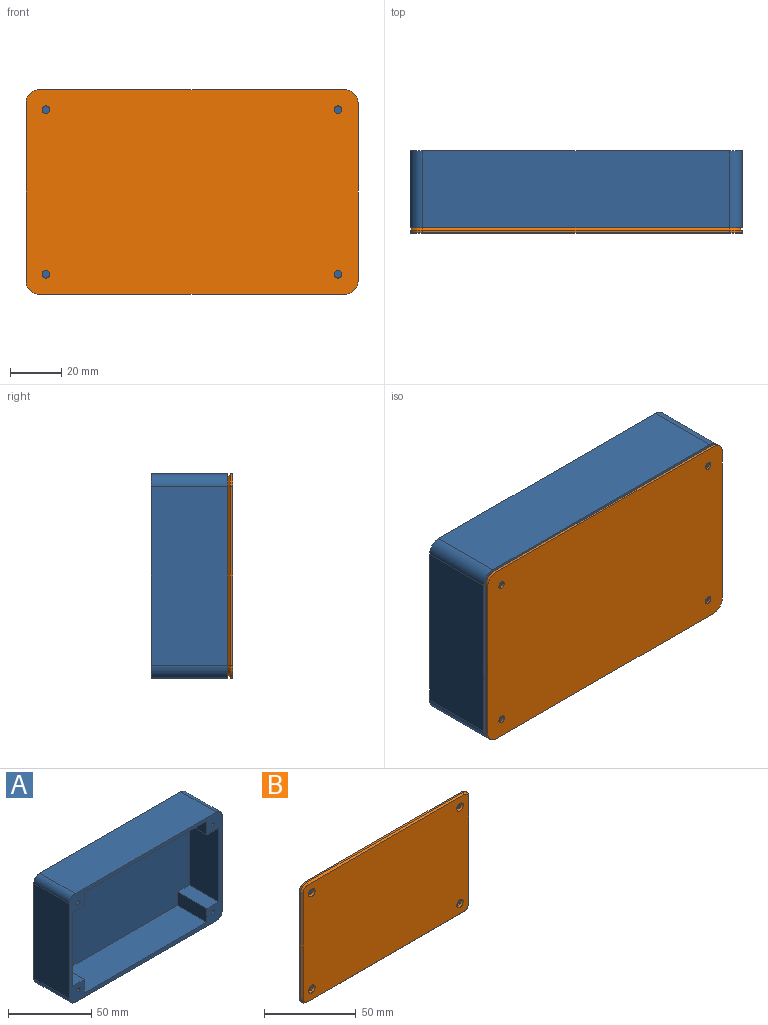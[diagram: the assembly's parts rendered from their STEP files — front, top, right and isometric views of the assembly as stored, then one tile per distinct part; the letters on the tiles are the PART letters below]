
ASSEMBLY  parts=2 mates=1
PART A: 31 faces, bbox 130x30x80 mm
  f0: plane 25x10mm, normal (1,0,0), area 250mm2, adj f1,f2,f5,f6
  f1: plane 25x10mm, normal (0,0,1), area 250mm2, adj f0,f2,f6,f21
  f2: plane 130x80mm, normal (0,-1,0), area 1494.9mm2, adj f0,f1,f3,f5,f7,f8,f9,f11
  f3: cylinder r=1.5mm len=10mm, axis (0,-1,0), area 94.2mm2, adj f2,f4
  f4: plane 3x3mm, normal (0,-1,0), area 7.1mm2, adj f3
  f5: plane 104.4x25mm, normal (0,0,1), area 2610mm2, adj f0,f2,f6,f12
  f6: plane 124.4x74.4mm, normal (0,-1,0), area 8855.4mm2, adj f0,f1,f5,f7,f8,f11,f12,f13
  f7: plane 25x10mm, normal (-1,0,0), area 250mm2, adj f2,f6,f8,f20
  f8: plane 25x10mm, normal (0,0,-1), area 250mm2, adj f2,f6,f7,f11
  f9: cylinder r=1.5mm len=10mm, axis (0,-1,0), area 94.2mm2, adj f2,f10
  f10: plane 3x3mm, normal (0,-1,0), area 7.1mm2, adj f9
  f11: plane 54.4x25mm, normal (-1,0,0), area 1360mm2, adj f2,f6,f8,f13
  f12: plane 25x10mm, normal (-1,0,0), area 250mm2, adj f2,f5,f6,f13
  f13: plane 25x10mm, normal (0,0,1), area 250mm2, adj f2,f6,f11,f12
  f14: cylinder r=1.5mm len=10mm, axis (0,-1,0), area 94.2mm2, adj f2,f15
  f15: plane 3x3mm, normal (0,-1,0), area 7.1mm2, adj f14
  f16: plane 25x10mm, normal (1,0,0), area 250mm2, adj f2,f6,f17,f20
  f17: plane 25x10mm, normal (0,0,-1), area 250mm2, adj f2,f6,f16,f21
  f18: cylinder r=1.5mm len=10mm, axis (0,-1,0), area 94.2mm2, adj f2,f19
  f19: plane 3x3mm, normal (0,-1,0), area 7.1mm2, adj f18
  f20: plane 104.4x25mm, normal (0,0,-1), area 2610mm2, adj f2,f6,f7,f16
  f21: plane 54.4x25mm, normal (1,0,0), area 1360mm2, adj f1,f2,f6,f17
  f22: cylinder r=5mm len=30mm, axis (0,1,0), area 235.6mm2, adj f2,f23,f29,f30
  f23: plane 120x30mm, normal (0,0,-1), area 3600mm2, adj f2,f22,f24,f30
  f24: cylinder r=5mm len=30mm, axis (0,1,0), area 235.6mm2, adj f2,f23,f25,f30
  f25: plane 70x30mm, normal (1,0,0), area 2100mm2, adj f2,f24,f26,f30
  f26: cylinder r=5mm len=30mm, axis (0,1,0), area 235.6mm2, adj f2,f25,f27,f30
  f27: plane 120x30mm, normal (0,0,1), area 3600mm2, adj f2,f26,f28,f30
  f28: cylinder r=5mm len=30mm, axis (0,1,0), area 235.6mm2, adj f2,f27,f29,f30
  f29: plane 70x30mm, normal (-1,0,0), area 2100mm2, adj f2,f22,f28,f30
  f30: plane 130x80mm, normal (0,1,0), area 10378.5mm2, adj f22,f23,f24,f25,f26,f27,f28,f29
PART B: 26 faces, bbox 130x2x80 mm
  f0: plane 120x1mm, normal (0,0,1), area 120mm2, adj f1,f11,f13,f19
  f1: cylinder r=5mm len=5mm, axis (0,1,0), area 7.9mm2, adj f0,f2,f13,f21
  f2: plane 70x1mm, normal (-1,0,0), area 70mm2, adj f1,f3,f13,f20
  f3: cylinder r=5mm len=5mm, axis (0,1,0), area 7.9mm2, adj f2,f4,f13,f18
  f4: plane 120x1mm, normal (0,0,-1), area 120mm2, adj f3,f5,f13,f16
  f5: cylinder r=5mm len=5mm, axis (0,1,0), area 7.9mm2, adj f4,f6,f13,f14
  f6: plane 70x1mm, normal (1,0,0), area 70mm2, adj f5,f11,f13,f15
  f7: cylinder r=1.5mm len=3mm, axis (0,1,0), area 9.4mm2, adj f13,f25
  f8: cylinder r=1.5mm len=3mm, axis (0,1,0), area 9.4mm2, adj f13,f24
  f9: cylinder r=1.5mm len=3mm, axis (0,1,0), area 9.4mm2, adj f13,f23
  f10: cylinder r=1.5mm len=3mm, axis (0,1,0), area 9.4mm2, adj f13,f22
  f11: cylinder r=5mm len=5mm, axis (0,1,0), area 7.9mm2, adj f0,f6,f13,f17
  f12: plane 128x78mm, normal (0,-1,0), area 9891.7mm2, adj f14,f15,f16,f17,f18,f19,f20,f21
  f13: plane 130x80mm, normal (0,1,0), area 10350.3mm2, adj f0,f1,f2,f3,f4,f5,f6,f7
  f14: cone r=4mm half-angle=45deg, axis (0,1,0), area 10mm2, adj f5,f12,f15,f16
  f15: plane 70x1mm, normal (0.71,-0.71,0), area 99mm2, adj f6,f12,f14,f17
  f16: plane 120x1mm, normal (0,-0.71,-0.71), area 169.7mm2, adj f4,f12,f14,f18
  f17: cone r=4mm half-angle=45deg, axis (0,1,0), area 10mm2, adj f11,f12,f15,f19
  f18: cone r=4mm half-angle=45deg, axis (0,1,0), area 10mm2, adj f3,f12,f16,f20
  f19: plane 120x1mm, normal (0,-0.71,0.71), area 169.7mm2, adj f0,f12,f17,f21
  f20: plane 70x1mm, normal (-0.71,-0.71,0), area 99mm2, adj f2,f12,f18,f21
  f21: cone r=4mm half-angle=45deg, axis (0,1,0), area 10mm2, adj f1,f12,f19,f20
  f22: cone r=1.5mm half-angle=45deg, axis (0,-1,0), area 17.8mm2, adj f10,f12
  f23: cone r=1.5mm half-angle=45deg, axis (0,-1,0), area 17.8mm2, adj f9,f12
  f24: cone r=1.5mm half-angle=45deg, axis (0,-1,0), area 17.8mm2, adj f8,f12
  f25: cone r=1.5mm half-angle=45deg, axis (0,-1,0), area 17.8mm2, adj f7,f12
PLACE A t=(-4.12,2.05,6.17)mm fixed
PLACE B rot(axis=(1,0,0),180deg) t=(-4.12,-82.25,6.17)mm
MATE slider A.f14 <-> B.f9  axis (0,-1,0) through (53.08,-27.95,-26.03)mm
